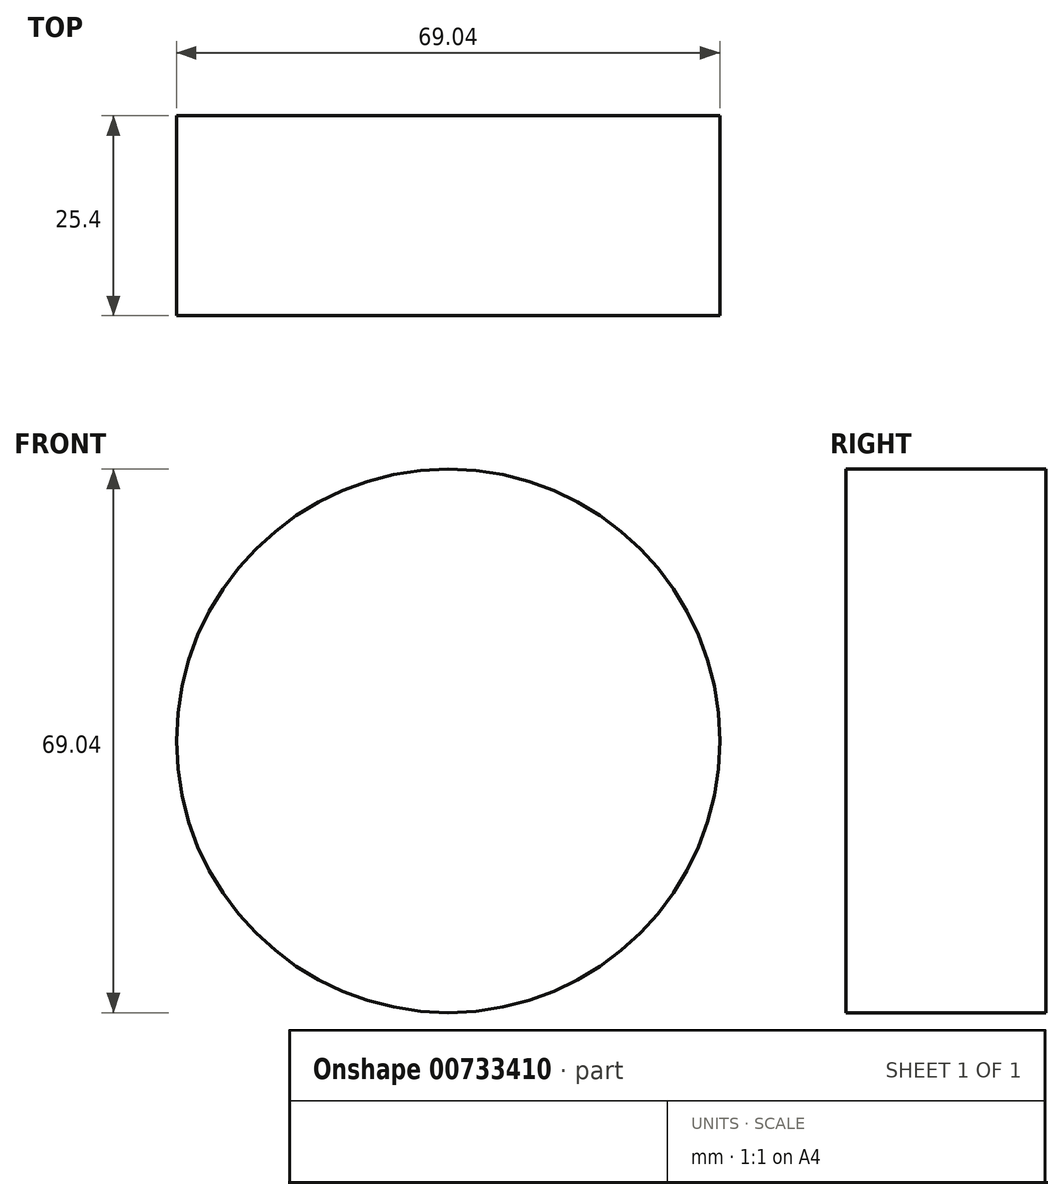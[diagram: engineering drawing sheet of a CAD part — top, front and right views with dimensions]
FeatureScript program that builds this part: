
annotation { "Feature Type Name" : "Feature", "Feature Type Description" : "" }
export const myFeature = defineFeature(function(context is Context, id is Id, definition is map)
    precondition{}
    {
        {
            var Q0;
            Q0=qCreatedBy(makeId("Front.planeOp"),FACE);
            var sketch = newSketch(context, id + "F0", { "sketchPlane" : qUnion([Q0])});
            skCircle(sketch, "E0", {"center": v(0, 0) * mm, "radius": 34.52 * mm});
            skSolve(sketch);
        }
        {
            var Q0;
            Q0 = qSketchRegion(id + "F0", true);
            extrude(context, id + "F1", {"entities" : qUnion([Q0]), "depth" : 25.4 * mm, "offsetDistance" : 25.4 * mm});
        }
    });
